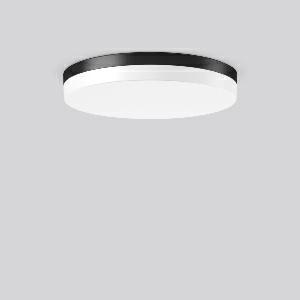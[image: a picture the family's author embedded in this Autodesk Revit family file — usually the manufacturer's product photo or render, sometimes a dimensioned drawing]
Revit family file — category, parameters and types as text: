
# Revit family: flat_slim_round_312634_0031_1_19_7e85
name_source: partatom
category: Lighting Fixtures
units: mm (PartAtom-declared; Revit-internal decimal feet)

## family parameters
Cut with Voids When Loaded = No
Host = Face
Light Source = No
Part Type = Normal
Room Calculation Point = No
Round Connector Dimension = Use Diameter
Shared = No

## types (1)
- MultiLumen 1 830 (1 x LED Modul 830, 3500 lm, 3000)
    Apparent Load = 24 VA
    CIE Flux Codes = 38 68 89 85 100
    Color Rendering = 80
    Color Temperature = 3000
    Default Elevation = 1800 mm
    Height = 70 mm
    Lamp = 1 x LED Modul 830
    Lamp Light Flux = 3500 lm
    Lamp count = 1
    Length = 480 mm
    Lifetime = 50000 h
    Luminous efficacy = 146 lm/W
    Manufacturer = RZB
    ModVariant = No
    Model = 312634.0031.1.19
    Mounting Place = Ceiling
    Mounting Type = Surface mounted
    Number of Poles = 1
    OnlyDefault = Yes
    Power Factor = 1
    Product Name = FLAT SLIM round
    Product group = Surface mounted ceiling and wall luminaires
    ProductGroupID = 305
    Protection Class = Protection class I
    Protection Degree = Degree of protection
    RLX_Detail_Level = 1
    RLX_Emergency_Light_Flux = 0 lm
    RLX_Emergency_Type = 0
    RLX_Emergency_Type_DB = No
    RlxData = <blob elided: 23657 chars, md5=14e510c1>
    Socket = socket
    Standby Power = 0 W
    System Light Flux = 3500 lm
    System Power = 24 W
    Type Comments = MultiLumen 1 830
    Type Image = 312633.0031.jpg
    URL = http://relux.com
    VarID = multilumen_1_830
    Voltage = 0 V
    Weight = 0.00 kg
    Width = 0 mm  [stored 0 ft]

note: [stored X ft] marks values corroborated as IEEE doubles in the binary element streams (Revit-internal decimal feet)

## geometry (parser evidence)
native form markers: Blend x4, Sweep x13
no freeform markers — native parametric forms only
